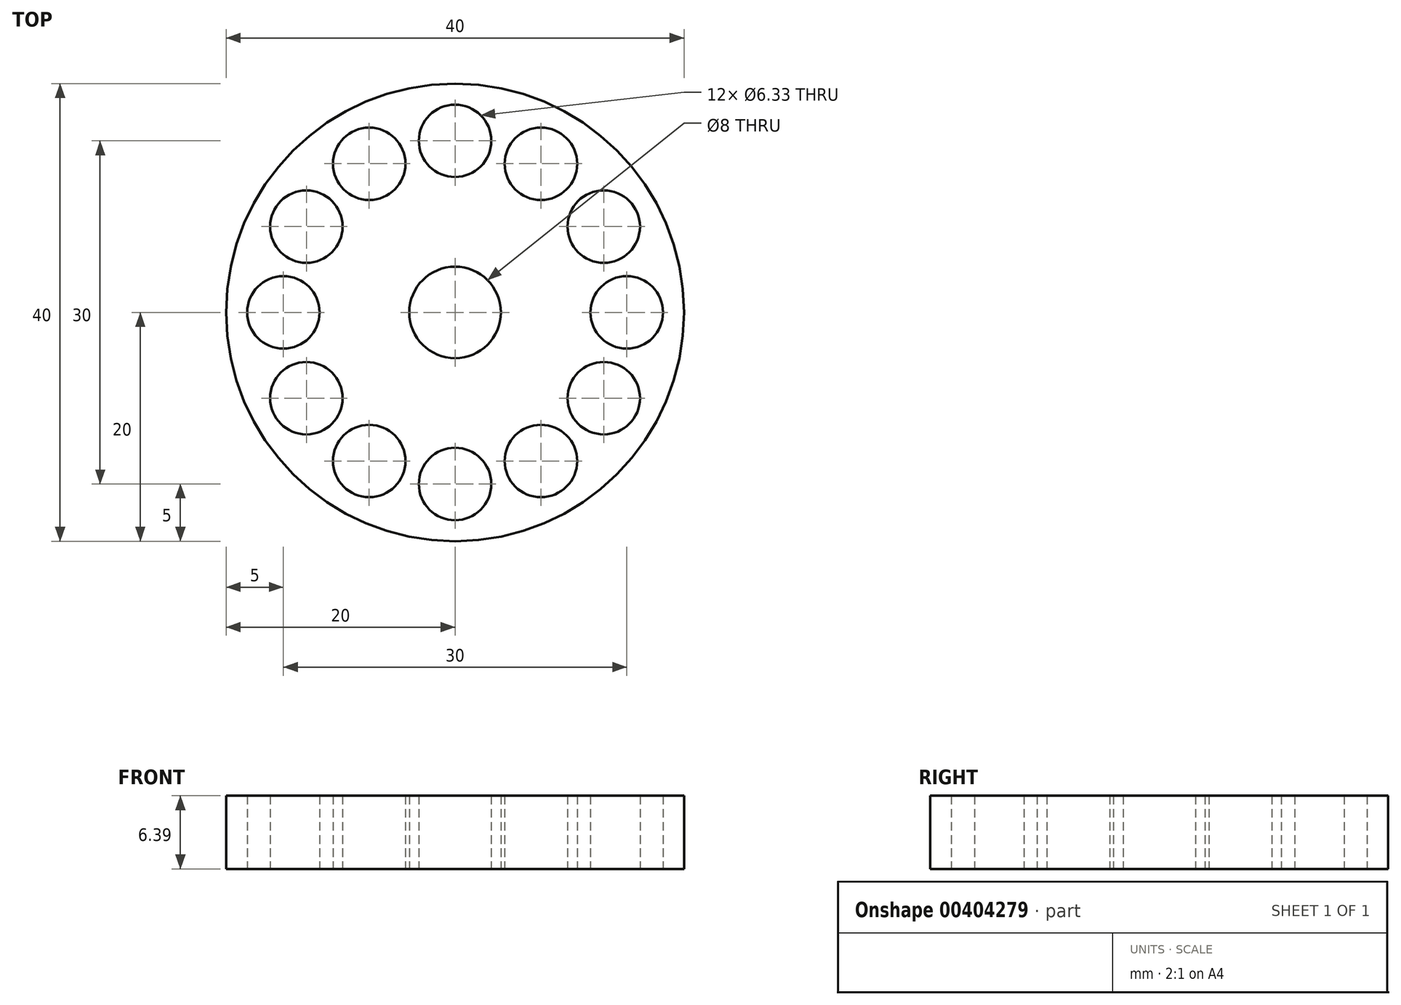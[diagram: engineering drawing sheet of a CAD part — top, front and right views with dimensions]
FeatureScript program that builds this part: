
annotation { "Feature Type Name" : "Feature", "Feature Type Description" : "" }
export const myFeature = defineFeature(function(context is Context, id is Id, definition is map)
    precondition{}
    {
        {
            var Q0;
            Q0=qCreatedBy(makeId("Top.planeOp"),FACE);
            var sketch = newSketch(context, id + "F0", { "sketchPlane" : qUnion([Q0])});
            skCircle(sketch, "E0", {"center": v(0, 0) * mm, "radius": 15 * mm, "construction": true});
            skCircle(sketch, "E1", {"center": v(15, 0) * mm, "radius": 3.17 * mm});
            skCircle(sketch, "E2.1.0", {"center": v(13, 7.5) * mm, "radius": 3.17 * mm});
            skCircle(sketch, "E2.2.0", {"center": v(7.5, 13) * mm, "radius": 3.17 * mm});
            skCircle(sketch, "E2.3.0", {"center": v(0, 15) * mm, "radius": 3.17 * mm});
            skCircle(sketch, "E2.4.0", {"center": v(-7.5, 13) * mm, "radius": 3.16 * mm});
            skCircle(sketch, "E2.5.0", {"center": v(-13, 7.5) * mm, "radius": 3.17 * mm});
            skCircle(sketch, "E2.6.0", {"center": v(-15, 0) * mm, "radius": 3.17 * mm});
            skCircle(sketch, "E2.7.0", {"center": v(-13, -7.5) * mm, "radius": 3.17 * mm});
            skCircle(sketch, "E2.8.0", {"center": v(-7.5, -13) * mm, "radius": 3.17 * mm});
            skCircle(sketch, "E3", {"center": v(0, 0) * mm, "radius": 20 * mm});
            skCircle(sketch, "E4", {"center": v(0, 0) * mm, "radius": 4 * mm});
            skCircle(sketch, "E5.1.9.0", {"center": v(0, -15) * mm, "radius": 3.17 * mm});
            skCircle(sketch, "E6.1.10.0", {"center": v(7.5, -13) * mm, "radius": 3.17 * mm});
            skCircle(sketch, "E7.1.11.0", {"center": v(13, -7.5) * mm, "radius": 3.17 * mm});
            skSolve(sketch);
        }
        {
            var Q0;
            Q0 = qSketchRegion(id + "F0", true);
            extrude(context, id + "F1", {"entities" : qUnion([Q0]), "depth" : 6.39 * mm});
        }
    });
